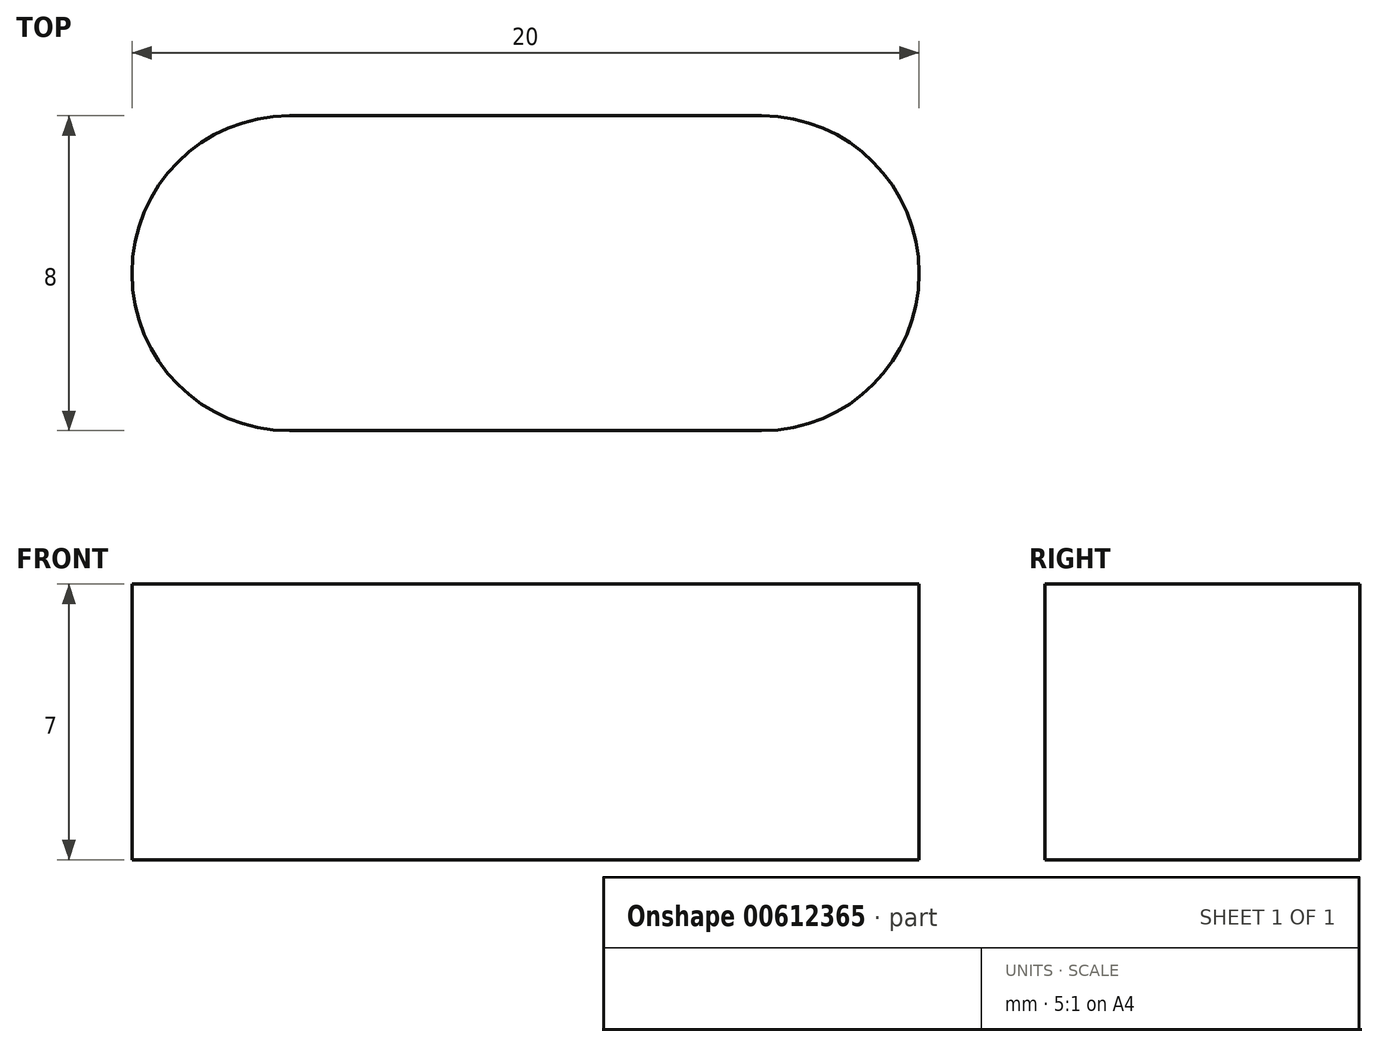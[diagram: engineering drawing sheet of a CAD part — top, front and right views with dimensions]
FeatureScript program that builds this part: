
annotation { "Feature Type Name" : "Feature", "Feature Type Description" : "" }
export const myFeature = defineFeature(function(context is Context, id is Id, definition is map)
    precondition{}
    {
        {
            var Q0;
            Q0=qCreatedBy(makeId("Top.planeOp"),FACE);
            var sketch = newSketch(context, id + "F0", { "sketchPlane" : qUnion([Q0])});
            skArc(sketch, "E0", {"start": v(0, 4) * mm, "mid": v(-4, 0) * mm, "end": v(0, -4) * mm});
            skArc(sketch, "E1", {"start": v(12, -4) * mm, "mid": v(16, 0) * mm, "end": v(12, 4) * mm});
            skLineSegment(sketch, "E2", {"start": v(0, 4) * mm, "end": v(12, 4) * mm});
            skLineSegment(sketch, "E3", {"start": v(12, -4) * mm, "end": v(0, -4) * mm});
            skSolve(sketch);
        }
        {
            var Q0;
            Q0=makeQuery(id+"F0.imprint","IMPRINT",FACE,{"disambiguationData":[TD([[makeQuery(id+"F0.imprint","IMPRINT",EDGE,{"derivedFrom":sQuery(id+"F0.wireOp",EDGE,"E0")}),1.0]])]});
            extrude(context, id + "F1", {"entities" : qUnion([Q0]), "depth" : 7 * mm, "offsetDistance" : 25 * mm});
        }
    });
